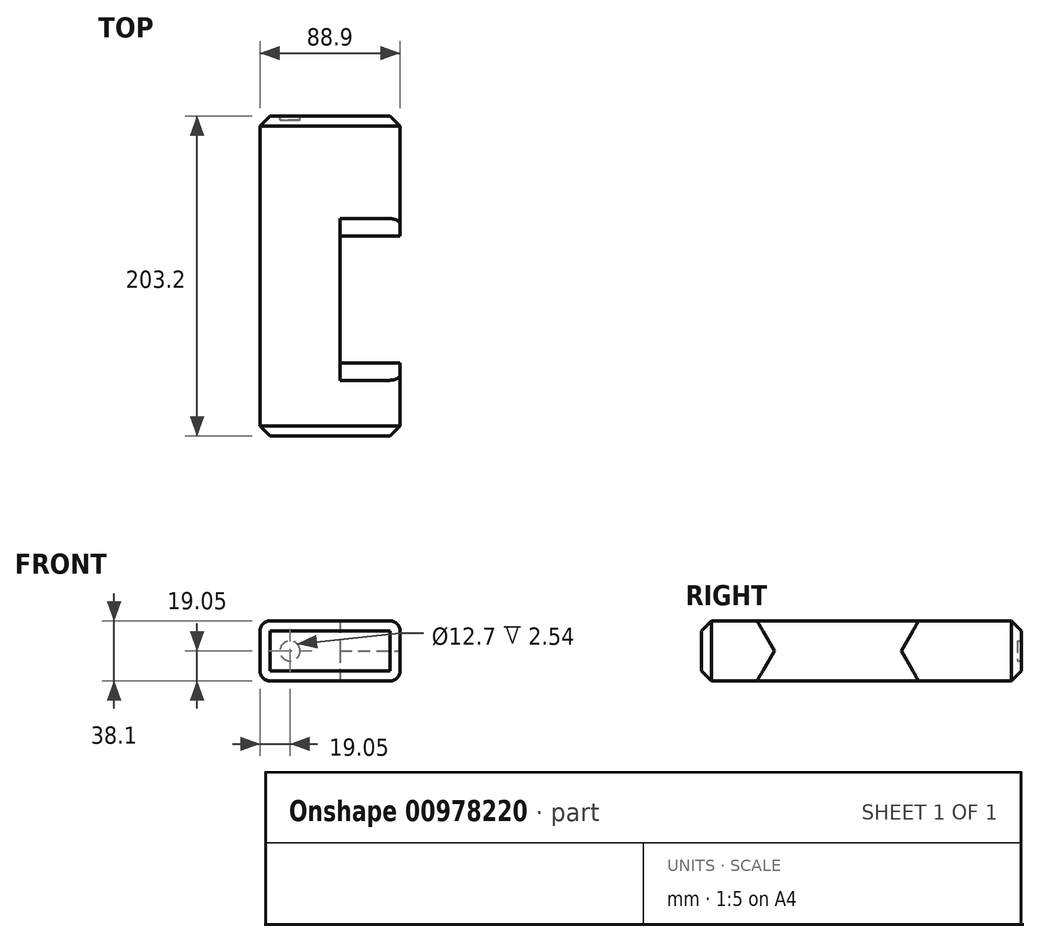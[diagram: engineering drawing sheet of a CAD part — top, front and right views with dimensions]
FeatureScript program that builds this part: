
annotation { "Feature Type Name" : "Feature", "Feature Type Description" : "" }
export const myFeature = defineFeature(function(context is Context, id is Id, definition is map)
    precondition{}
    {
        {
            var Q0;
            Q0=qCreatedBy(makeId("Front.planeOp"),FACE);
            var sketch = newSketch(context, id + "F0", { "sketchPlane" : qUnion([Q0])});
            skLineSegment(sketch, "E0.bottom", {"start": v(-44.45, 19.05) * mm, "end": v(44.45, 19.05) * mm});
            skLineSegment(sketch, "E0.top", {"start": v(-44.45, -19.05) * mm, "end": v(44.45, -19.05) * mm});
            skLineSegment(sketch, "E0.left", {"start": v(-44.45, 19.05) * mm, "end": v(-44.45, -19.05) * mm});
            skLineSegment(sketch, "E0.right", {"start": v(44.45, 19.05) * mm, "end": v(44.45, -19.05) * mm});
            skLineSegment(sketch, "E1", {"start": v(0, 0) * mm, "end": v(0, 19.05) * mm, "construction": true});
            skLineSegment(sketch, "E2", {"start": v(0, 0) * mm, "end": v(44.45, 0) * mm, "construction": true});
            skSolve(sketch);
        }
        {
            var Q0;
            Q0=makeQuery(id+"F0.imprint","IMPRINT",FACE,{"disambiguationData":[TD([[makeQuery(id+"F0.imprint","IMPRINT",EDGE,{"derivedFrom":sQuery(id+"F0.wireOp",EDGE,"E0.bottom")}),-1.0]])]});
            extrude(context, id + "F1", {"entities" : qUnion([Q0]), "depth" : 203.2 * mm, "offsetDistance" : 25.4 * mm});
        }
        {
            var Q0;
            Q0=makeQuery(id+"F1.opExtrude","SWEPT_EDGE",EDGE,{"disambiguationData":[OSD([sQuery(id+"F0.wireOp",EDGE,"E0.bottom"),sQuery(id+"F0.wireOp",EDGE,"E0.left")])]});
            var Q1;
            Q1=makeQuery(id+"F1.opExtrude","SWEPT_EDGE",EDGE,{"disambiguationData":[OSD([sQuery(id+"F0.wireOp",EDGE,"E0.top"),sQuery(id+"F0.wireOp",EDGE,"E0.left")])]});
            var Q2;
            Q2=makeQuery(id+"F1.opExtrude","SWEPT_EDGE",EDGE,{"disambiguationData":[OSD([sQuery(id+"F0.wireOp",EDGE,"E0.bottom"),sQuery(id+"F0.wireOp",EDGE,"E0.right")])]});
            var Q3;
            Q3=makeQuery(id+"F1.opExtrude","SWEPT_EDGE",EDGE,{"disambiguationData":[OSD([sQuery(id+"F0.wireOp",EDGE,"E0.top"),sQuery(id+"F0.wireOp",EDGE,"E0.right")])]});
            fillet(context, id + "F2", {"entities" : qUnion([Q0, Q1, Q2, Q3]), "radius" : 6.35 * mm, "tangentPropagation" : true, "allowEdgeOverflow" : false});
        }
        {
            var Q0;
            Q0=makeQuery(id+"F1.opExtrude","CAP_EDGE",EDGE,{"disambiguationData":[OSD([sQuery(id+"F0.wireOp",EDGE,"E0.bottom")])],"isStart":false});
            chamfer(context, id + "F3", {"entities" : qUnion([Q0]), "width" : 6.35 * mm, "tangentPropagation" : true});
        }
        {
            var Q0;
            Q0=makeQuery(id+"F1.opExtrude","CAP_EDGE",EDGE,{"disambiguationData":[OSD([sQuery(id+"F0.wireOp",EDGE,"E0.bottom")])],"isStart":true});
            chamfer(context, id + "F4", {"entities" : qUnion([Q0]), "width" : 6.35 * mm, "tangentPropagation" : true});
        }
        {
            var Q0;
            Q0=makeQuery(id+"F1.opExtrude","SWEPT_FACE",FACE,{"disambiguationData":[OSD([sQuery(id+"F0.wireOp",EDGE,"E0.right")])]});
            var sketch = newSketch(context, id + "F5", { "sketchPlane" : qUnion([Q0])});
            skLineSegment(sketch, "E3", {"start": v(-76.2, 0) * mm, "end": v(-46.87, -50.8) * mm});
            skLineSegment(sketch, "E4", {"start": v(-186.17, 50.8) * mm, "end": v(-156.84, 0) * mm});
            skLineSegment(sketch, "E5", {"start": v(-76.2, 0) * mm, "end": v(-156.84, 0) * mm});
            skLineSegment(sketch, "E6", {"start": v(-76.2, 0) * mm, "end": v(-46.87, 50.8) * mm});
            skLineSegment(sketch, "E7", {"start": v(-156.84, 0) * mm, "end": v(-186.17, -50.8) * mm});
            skLineSegment(sketch, "E8", {"start": v(-46.87, 50.8) * mm, "end": v(-186.17, 50.8) * mm});
            skLineSegment(sketch, "E9", {"start": v(-186.17, -50.8) * mm, "end": v(-46.87, -50.8) * mm});
            skSolve(sketch);
        }
        {
            var Q0;
            Q0 = qSketchRegion(id + "F5", true);
            extrude(context, id + "F6", {"entities" : qUnion([Q0]), "operationType" : NewBodyOperationType.REMOVE, "oppositeDirection" : true, "depth" : 38.1 * mm, "offsetDistance" : 25.4 * mm});
        }
        {
            var Q0;
            Q0=makeQuery(id+"F1.opExtrude","CAP_FACE",FACE,{"disambiguationData":[OSD([sQuery(id+"F0.wireOp",EDGE,"E0.bottom"),sQuery(id+"F0.wireOp",EDGE,"E0.top"),sQuery(id+"F0.wireOp",EDGE,"E0.left"),sQuery(id+"F0.wireOp",EDGE,"E0.right")])],"isStart":true});
            var sketch = newSketch(context, id + "F7", { "sketchPlane" : qUnion([Q0])});
            skCircle(sketch, "E10", {"center": v(25.4, 0) * mm, "radius": 6.35 * mm});
            skSolve(sketch);
        }
        {
            var Q0;
            Q0 = qSketchRegion(id + "F7", true);
            extrude(context, id + "F8", {"entities" : qUnion([Q0]), "operationType" : NewBodyOperationType.REMOVE, "oppositeDirection" : true, "depth" : 2.54 * mm, "offsetDistance" : 25.4 * mm});
        }
    });
